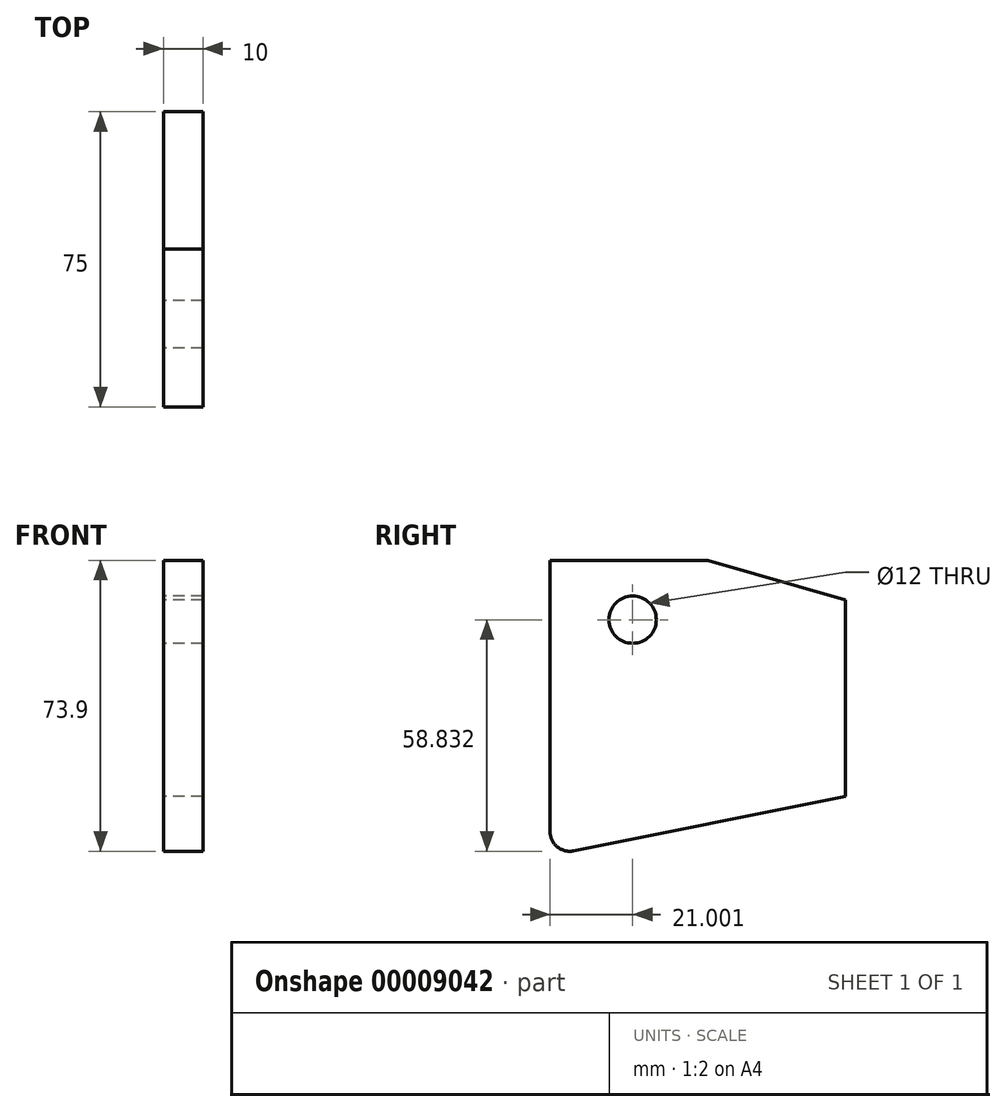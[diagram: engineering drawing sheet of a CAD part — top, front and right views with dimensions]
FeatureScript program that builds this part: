
annotation { "Feature Type Name" : "Feature", "Feature Type Description" : "" }
export const myFeature = defineFeature(function(context is Context, id is Id, definition is map)
    precondition{}
    {
        {
            var Q0;
            Q0=qCreatedBy(makeId("Right.planeOp"),FACE);
            var sketch = newSketch(context, id + "F0", { "sketchPlane" : qUnion([Q0])});
            skLineSegment(sketch, "E0.top", {"start": v(82.98, -26.14) * mm, "end": v(7.98, -26.14) * mm});
            skLineSegment(sketch, "E0.right", {"start": v(7.98, 33.86) * mm, "end": v(7.98, -26.14) * mm});
            skLineSegment(sketch, "E1", {"start": v(82.98, -26.14) * mm, "end": v(82.98, 23.86) * mm});
            skLineSegment(sketch, "E2", {"start": v(82.98, 23.86) * mm, "end": v(48.14, 33.86) * mm});
            skLineSegment(sketch, "E3", {"start": v(48.14, 33.86) * mm, "end": v(7.98, 33.86) * mm});
            skLineSegment(sketch, "E4.bottom", {"start": v(7.98, -26.14) * mm, "end": v(82.98, -26.14) * mm});
            skLineSegment(sketch, "E5", {"start": v(7.98, -26.14) * mm, "end": v(7.98, -41.14) * mm});
            skLineSegment(sketch, "E6", {"start": v(7.98, -41.14) * mm, "end": v(82.98, -26.14) * mm});
            skSolve(sketch);
        }
        {
            var Q0;
            Q0 = qSketchRegion(id + "F0", true);
            extrude(context, id + "F1", {"entities" : qUnion([Q0]), "depth" : 10 * mm});
        }
        {
            var Q0;
            Q0=makeQuery(id+"F1.opExtrude","CAP_FACE",FACE,{"disambiguationData":[OSD([sQuery(id+"F0.wireOp",EDGE,"E0.bottom"),sQuery(id+"F0.wireOp",EDGE,"E0.top"),sQuery(id+"F0.wireOp",EDGE,"E0.left"),sQuery(id+"F0.wireOp",EDGE,"E0.right")])],"isStart":true});
            var sketch = newSketch(context, id + "F2", { "sketchPlane" : qUnion([Q0])});
            skCircle(sketch, "E7", {"center": v(-28.98, 18.8) * mm, "radius": 6 * mm});
            skLineSegment(sketch, "E8", {"start": v(-28.98, 18.8) * mm, "end": v(-28.98, -31.2) * mm, "construction": true});
            skSolve(sketch);
        }
        {
            var Q0;
            Q0 = qSketchRegion(id + "F2", true);
            extrude(context, id + "F3", {"entities" : qUnion([Q0]), "operationType" : NewBodyOperationType.REMOVE, "endBound" : BoundingType.THROUGH_ALL, "oppositeDirection" : true, "depth" : 25 * mm});
        }
        {
            var Q0;
            Q0=makeQuery(id+"F1.opExtrude","SWEPT_EDGE",EDGE,{"disambiguationData":[OSD([sQuery(id+"F0.wireOp",EDGE,"E5"),sQuery(id+"F0.wireOp",EDGE,"E6")])]});
            fillet(context, id + "F4", {"entities" : qUnion([Q0]), "radius" : 5 * mm, "tangentPropagation" : true, "allowEdgeOverflow" : false});
        }
    });
